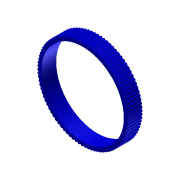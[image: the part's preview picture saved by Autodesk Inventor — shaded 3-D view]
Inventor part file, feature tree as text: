
AUTODESK INVENTOR PART (.ipt)
format: ipt  version: 2011 (Build 150239000, 239)  size: 665,600 bytes
history: native  units: in
note: dims shown in document units (in); Inventor stores cm internally (conversion verified against a paired STEP export)
features: extrude x2, sketch x2, pattern_circular x1
ambient origin geometry x8: Origin, YZ Plane, XZ Plane, XY Plane, X Axis, Y Axis, Z Axis, Center Point
bodies: Solid1 (feature_tree)
feature tree (5):
  extrude  "Extrusion1"  Depth=6.05in
  extrude  "Extrusion2"  Depth=0.0137in
  pattern_circular  "Circular Pattern1"  [2 undecoded]
  sketch  "Sketch1"  dims[d0=5.6in d1=6.05in]
  sketch  "Sketch2"  dims[d2=1.0in d3=0.0in d4=0.0137in d7=0.05in d8=0.025in d10=0.0137in d11=0.025in d12=0.025in d13=1.0in d14=0.0in d15=35.4331in d16=360.0deg]
note: 2 required parameter values undecoded (feature->parameter linkage not recoverable at this tier; creation-order binding heuristic only, values carry confidence <= 0.55)
